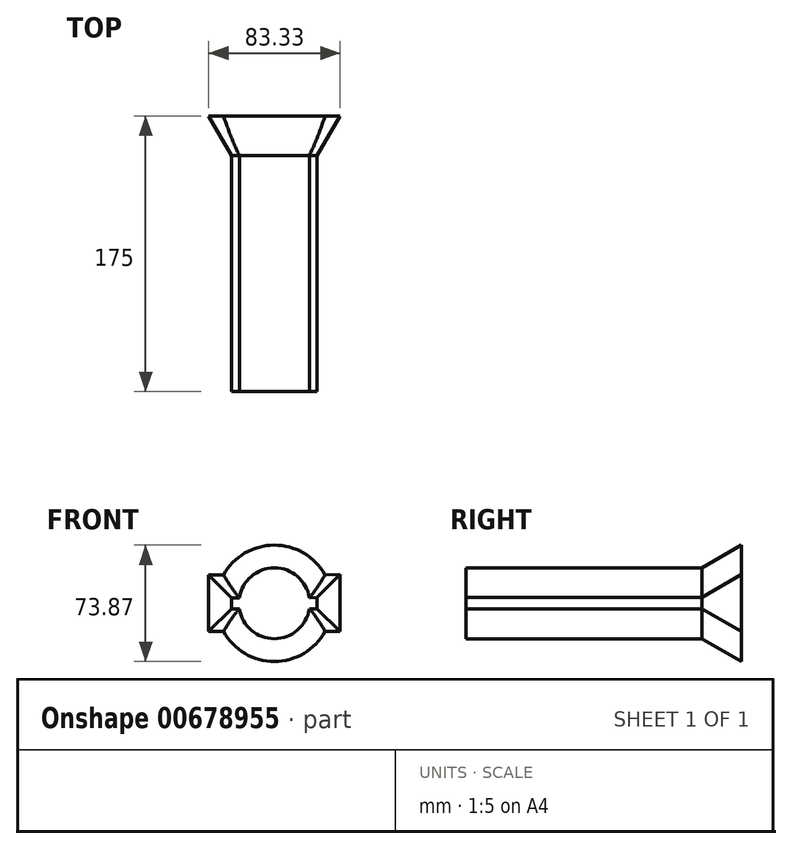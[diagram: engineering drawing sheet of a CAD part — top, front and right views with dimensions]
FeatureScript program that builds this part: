
annotation { "Feature Type Name" : "Feature", "Feature Type Description" : "" }
export const myFeature = defineFeature(function(context is Context, id is Id, definition is map)
    precondition{}
    {
        {
            var Q0;
            Q0=qCreatedBy(makeId("Front.planeOp"),FACE);
            var sketch = newSketch(context, id + "F0", { "sketchPlane" : qUnion([Q0])});
            skCircle(sketch, "E0", {"center": v(0, -0.02) * mm, "radius": 22.5 * mm});
            skLineSegment(sketch, "E1", {"start": v(-22.23, 3.48) * mm, "end": v(-27.23, 3.48) * mm});
            skLineSegment(sketch, "E2", {"start": v(-27.23, 3.48) * mm, "end": v(-27.23, -3.52) * mm});
            skLineSegment(sketch, "E3", {"start": v(-27.23, -3.52) * mm, "end": v(-22.23, -3.52) * mm});
            skLineSegment(sketch, "E4", {"start": v(22.23, -3.46) * mm, "end": v(27.23, -3.46) * mm});
            skLineSegment(sketch, "E5", {"start": v(27.23, -3.46) * mm, "end": v(27.23, 3.54) * mm});
            skLineSegment(sketch, "E6", {"start": v(27.23, 3.54) * mm, "end": v(22.23, 3.41) * mm});
            skSolve(sketch);
        }
        {
            var Q0;
            {var subQ0=sQuery(id+"F0.wireOp",EDGE,"E0");var subQ1=makeQuery(id+"F0.imprint","INTERSECT",VERTEX,{"derivedFrom":[subQ0,sQuery(id+"F0.wireOp",EDGE,"E1")]});Q0=makeQuery(id+"F0.imprint","IMPRINT",FACE,{"disambiguationData":[TD([[makeQuery(id+"F0.imprint","IMPRINT",EDGE,{"disambiguationData":[TD([[subQ1,1.0]])],"derivedFrom":subQ0}),1.0]])]});}
            var Q1;
            {var subQ0=sQuery(id+"F0.wireOp",EDGE,"E1");Q1=makeQuery(id+"F0.imprint","IMPRINT",FACE,{"disambiguationData":[TD([[makeQuery(id+"F0.imprint","IMPRINT",EDGE,{"derivedFrom":subQ0}),1.0]])]});}
            var Q2;
            {var subQ0=sQuery(id+"F0.wireOp",EDGE,"E4");Q2=makeQuery(id+"F0.imprint","IMPRINT",FACE,{"disambiguationData":[TD([[makeQuery(id+"F0.imprint","IMPRINT",EDGE,{"derivedFrom":subQ0}),1.0]])]});}
            extrude(context, id + "F1", {"entities" : qUnion([Q0, Q1, Q2]), "depth" : 150 * mm, "offsetDistance" : 25 * mm});
        }
        {
            var Q0;
            Q0=makeQuery(id+"F1.opExtrude","CAP_FACE",FACE,{"disambiguationData":[OSD([sQuery(id+"F0.wireOp",EDGE,"E0"),sQuery(id+"F0.wireOp",EDGE,"E1"),sQuery(id+"F0.wireOp",EDGE,"E2"),sQuery(id+"F0.wireOp",EDGE,"E3"),sQuery(id+"F0.wireOp",EDGE,"E4"),sQuery(id+"F0.wireOp",EDGE,"E5"),sQuery(id+"F0.wireOp",EDGE,"E6")])],"isStart":true});
            extrude(context, id + "F2", {"entities" : qUnion([Q0]), "operationType" : NewBodyOperationType.ADD, "depth" : 25 * mm, "offsetDistance" : 25 * mm, "hasDraft" : true, "draftAngle" : 30 * degree});
        }
    });
